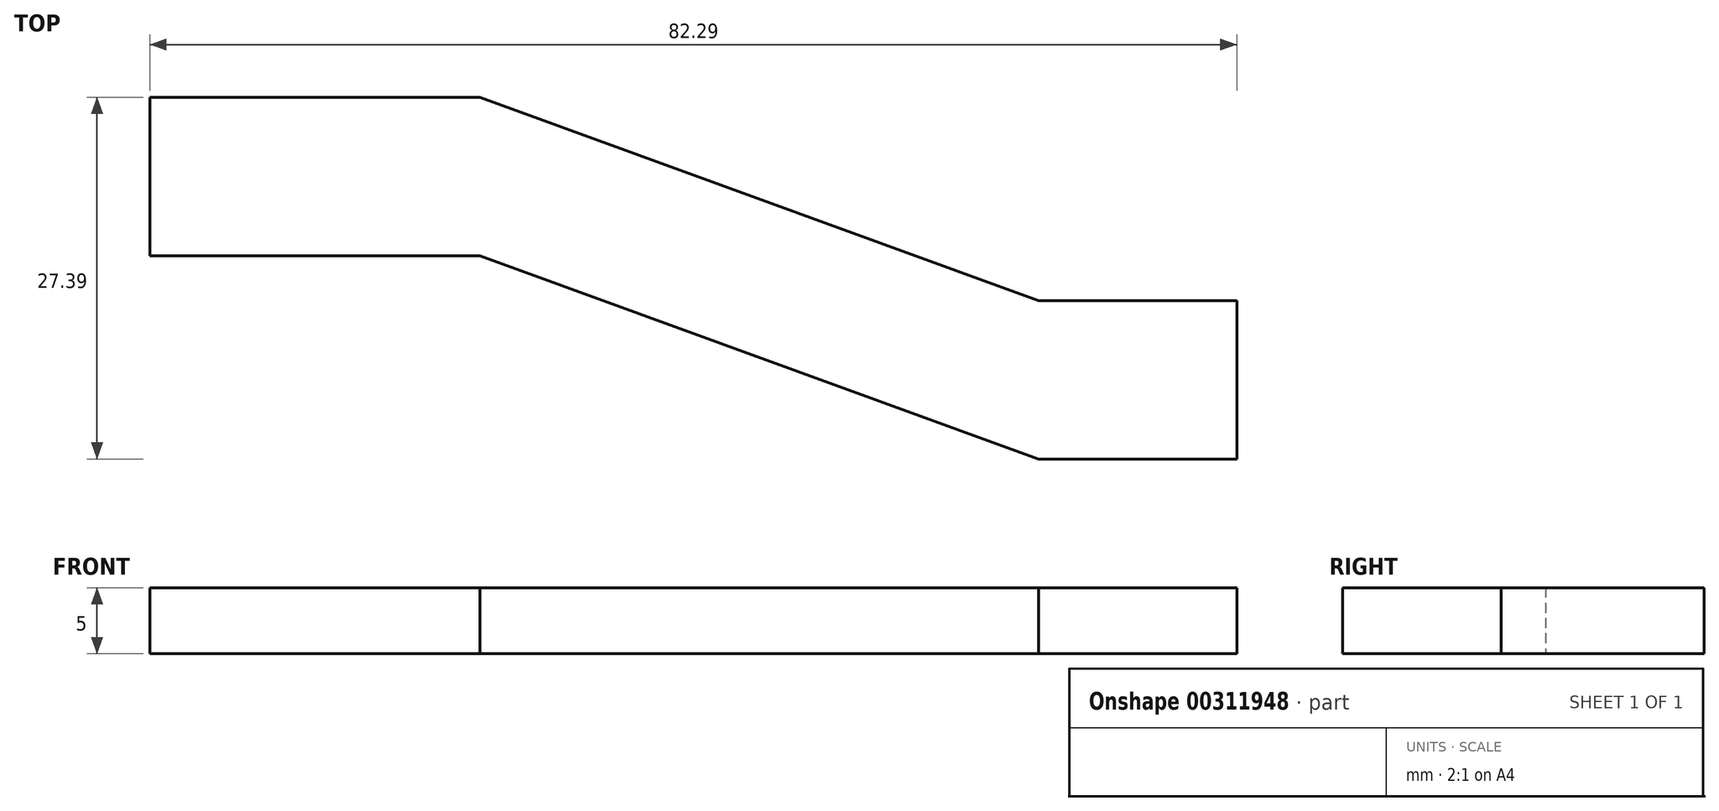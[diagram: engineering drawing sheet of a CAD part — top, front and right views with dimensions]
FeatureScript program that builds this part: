
annotation { "Feature Type Name" : "Feature", "Feature Type Description" : "" }
export const myFeature = defineFeature(function(context is Context, id is Id, definition is map)
    precondition{}
    {
        {
            var Q0;
            Q0=qCreatedBy(makeId("Top.planeOp"),FACE);
            var sketch = newSketch(context, id + "F0", { "sketchPlane" : qUnion([Q0])});
            skLineSegment(sketch, "E0.bottom", {"start": v(0, 0) * mm, "end": v(25, 0) * mm});
            skLineSegment(sketch, "E0.top", {"start": v(0, -12) * mm, "end": v(25, -12) * mm});
            skLineSegment(sketch, "E0.left", {"start": v(0, 0) * mm, "end": v(0, -12) * mm});
            skLineSegment(sketch, "E0.right", {"start": v(25, 0) * mm, "end": v(25, -12) * mm});
            skLineSegment(sketch, "E1.bottom", {"start": v(67.29, -15.4) * mm, "end": v(82.29, -15.4) * mm});
            skLineSegment(sketch, "E1.top", {"start": v(67.29, -27.4) * mm, "end": v(82.29, -27.4) * mm});
            skLineSegment(sketch, "E1.left", {"start": v(67.29, -15.4) * mm, "end": v(67.29, -27.4) * mm});
            skLineSegment(sketch, "E1.right", {"start": v(82.29, -15.4) * mm, "end": v(82.29, -27.4) * mm});
            skLineSegment(sketch, "E2", {"start": v(25, 0) * mm, "end": v(67.29, -15.4) * mm});
            skLineSegment(sketch, "E3", {"start": v(67.29, -27.4) * mm, "end": v(25, -12) * mm});
            skSolve(sketch);
        }
        {
            var Q0;
            Q0=makeQuery(id+"F0.imprint","IMPRINT",FACE,{"disambiguationData":[TD([[makeQuery(id+"F0.imprint","IMPRINT",EDGE,{"derivedFrom":sQuery(id+"F0.wireOp",EDGE,"E1.bottom")}),-1.0]])]});
            var Q1;
            Q1=makeQuery(id+"F0.imprint","IMPRINT",FACE,{"disambiguationData":[TD([[makeQuery(id+"F0.imprint","IMPRINT",EDGE,{"derivedFrom":sQuery(id+"F0.wireOp",EDGE,"E0.right")}),1.0]])]});
            var Q2;
            Q2=makeQuery(id+"F0.imprint","IMPRINT",FACE,{"disambiguationData":[TD([[makeQuery(id+"F0.imprint","IMPRINT",EDGE,{"derivedFrom":sQuery(id+"F0.wireOp",EDGE,"E0.bottom")}),-1.0]])]});
            extrude(context, id + "F1", {"entities" : qUnion([Q0, Q1, Q2]), "depth" : 5 * mm});
        }
    });
